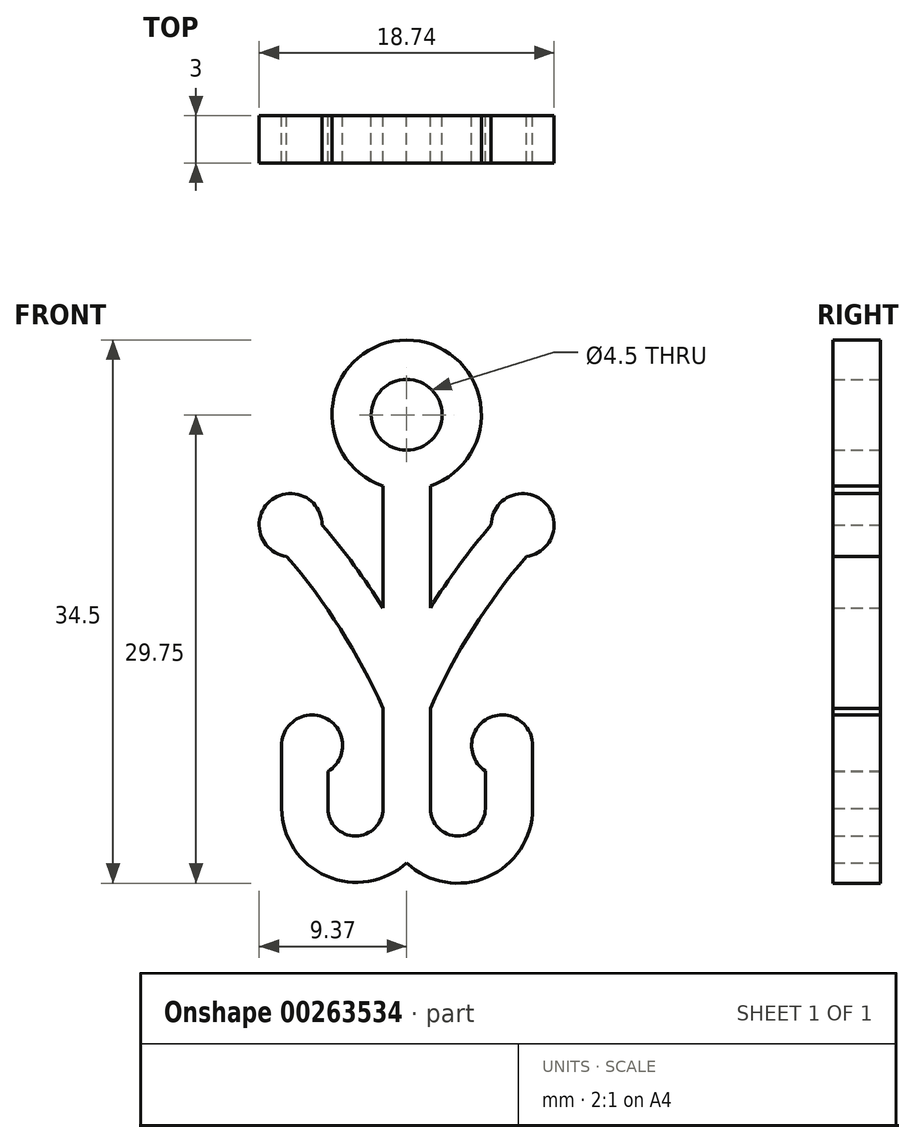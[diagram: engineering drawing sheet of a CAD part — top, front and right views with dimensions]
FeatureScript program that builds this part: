
annotation { "Feature Type Name" : "Feature", "Feature Type Description" : "" }
export const myFeature = defineFeature(function(context is Context, id is Id, definition is map)
    precondition{}
    {
        {
            var Q0;
            Q0=qCreatedBy(makeId("Front.planeOp"),FACE);
            var sketch = newSketch(context, id + "F1", { "sketchPlane" : qUnion([Q0])});
            skCircle(sketch, "E0", {"center": v(0, 0) * mm, "radius": 2.25 * mm});
            skArc(sketch, "E1", {"start": v(1.5, -4.5) * mm, "mid": v(0, 4.75) * mm, "end": v(-1.5, -4.5) * mm});
            skLineSegment(sketch, "E2", {"start": v(1.5, -4.5) * mm, "end": v(1.5, -12.27) * mm});
            skArc(sketch, "E3", {"start": v(-5, -25) * mm, "mid": v(-3.25, -26.75) * mm, "end": v(-1.5, -25) * mm});
            skArc(sketch, "E4", {"start": v(1.5, -25) * mm, "mid": v(3.25, -26.75) * mm, "end": v(5, -25) * mm});
            skArc(sketch, "E5", {"start": v(0, -28.46) * mm, "mid": v(5.14, -29.36) * mm, "end": v(8, -25) * mm});
            skPoint(sketch, "E6.end.orphan", {"position": v(-5, -25) * mm});
            skPoint(sketch, "E7.end.orphan", {"position": v(5, -25) * mm});
            skPoint(sketch, "E8.startSnap0", {"position": v(-6.03, -25) * mm});
            skLineSegment(sketch, "E9", {"start": v(-7.94, -25) * mm, "end": v(-7.94, -21) * mm});
            skLineSegment(sketch, "E10", {"start": v(8, -25) * mm, "end": v(8, -21) * mm});
            skArc(sketch, "E11", {"start": v(-5, -22.66) * mm, "mid": v(-5.05, -19.31) * mm, "end": v(-7.94, -21) * mm});
            skArc(sketch, "E12", {"start": v(8, -21) * mm, "mid": v(5.14, -19.3) * mm, "end": v(5, -22.62) * mm});
            skPoint(sketch, "E13.orphan", {"position": v(-6.03, -9.04) * mm});
            skArc(sketch, "E14.trimOffspring", {"start": v(-7.94, -25) * mm, "mid": v(-5.09, -29.3) * mm, "end": v(0, -28.46) * mm});
            skLineSegment(sketch, "E15", {"start": v(-5, -25) * mm, "end": v(-5, -22.66) * mm});
            skLineSegment(sketch, "E16", {"start": v(5, -25) * mm, "end": v(5, -22.62) * mm});
            skPoint(sketch, "E17.start.orphan", {"position": v(-4.13, -25) * mm});
            skPoint(sketch, "E18.orphan", {"position": v(4.12, -25) * mm});
            skPoint(sketch, "E19.orphan", {"position": v(5.62, -25) * mm});
            skLineSegment(sketch, "E20.trimOffspring", {"start": v(-1.5, -4.5) * mm, "end": v(-1.5, -12.27) * mm});
            skPoint(sketch, "E21.start.orphan", {"position": v(-1.5, 0) * mm});
            skPoint(sketch, "E22.orphan", {"position": v(1.5, 0) * mm});
            skArc(sketch, "E23", {"start": v(7.62, -8.98) * mm, "mid": v(4.21, -13.6) * mm, "end": v(1.5, -18.64) * mm});
            skArc(sketch, "E24", {"start": v(5.37, -7) * mm, "mid": v(3.33, -9.56) * mm, "end": v(1.5, -12.27) * mm});
            skLineSegment(sketch, "E25", {"start": v(-5.37, -7) * mm, "end": v(-5.37, -7) * mm});
            skArc(sketch, "E26", {"start": v(-5.37, -7) * mm, "mid": v(-8.7, -5.5) * mm, "end": v(-7.62, -8.98) * mm});
            skArc(sketch, "E27", {"start": v(7.62, -8.98) * mm, "mid": v(8.7, -5.5) * mm, "end": v(5.37, -7) * mm});
            skLineSegment(sketch, "E28.trimOffspring", {"start": v(5.37, -7) * mm, "end": v(5.37, -7) * mm});
            skArc(sketch, "E29.trimOffspring", {"start": v(-1.5, -12.27) * mm, "mid": v(-3.33, -9.56) * mm, "end": v(-5.37, -7) * mm});
            skArc(sketch, "E30.trimOffspring", {"start": v(-1.5, -18.64) * mm, "mid": v(-4.21, -13.6) * mm, "end": v(-7.62, -8.98) * mm});
            skLineSegment(sketch, "E31.trimOffspring", {"start": v(-1.5, -18.64) * mm, "end": v(-1.5, -25) * mm});
            skLineSegment(sketch, "E32.trimOffspring", {"start": v(1.5, -18.64) * mm, "end": v(1.5, -25) * mm});
            skSolve(sketch);
        }
        {
            var Q0;
            Q0=qSketchRegion(id+"F1",true);
            extrude(context, id + "F0", {"entities" : qUnion([Q0]), "depth" : 3 * mm});
        }
    });
